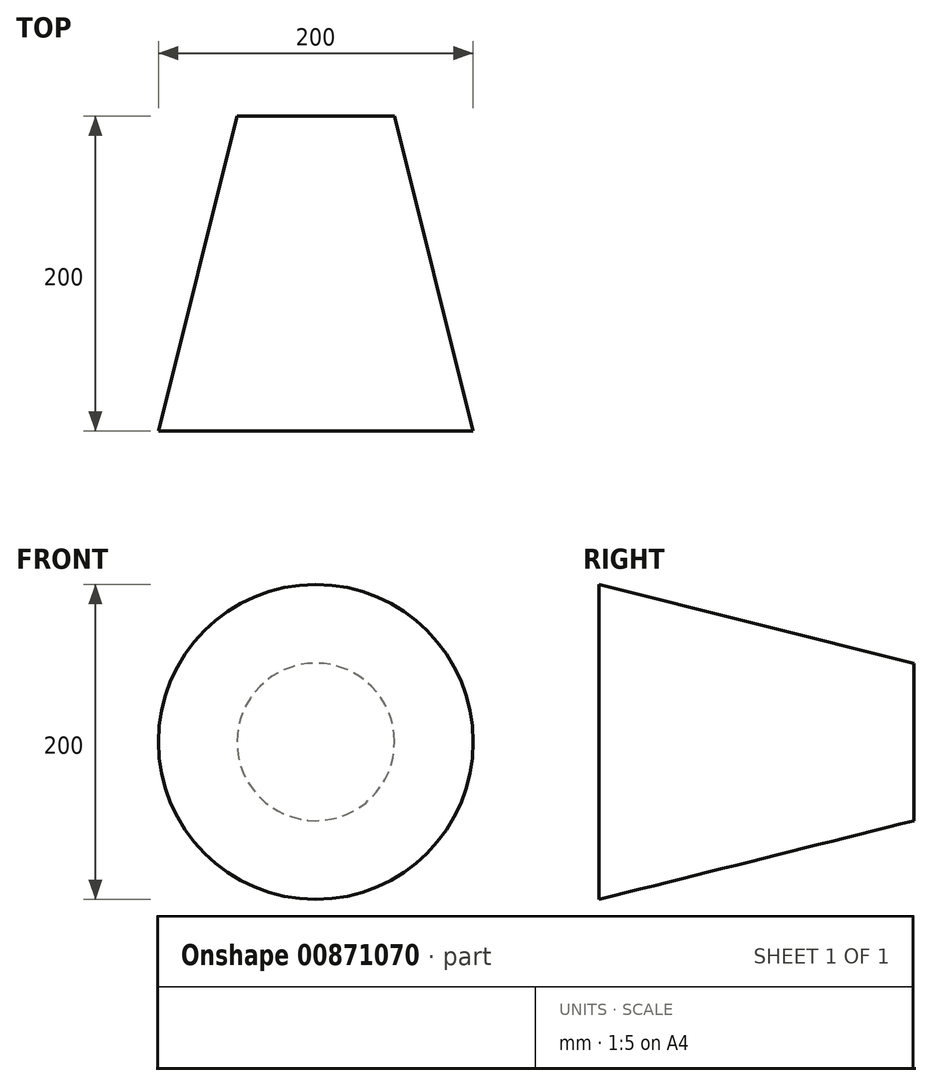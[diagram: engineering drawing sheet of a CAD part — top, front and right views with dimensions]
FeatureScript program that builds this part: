
annotation { "Feature Type Name" : "Feature", "Feature Type Description" : "" }
export const myFeature = defineFeature(function(context is Context, id is Id, definition is map)
    precondition{}
    {
        {
            var Q0;
            Q0=qCreatedBy(makeId("Right.planeOp"),FACE);
            var sketch = newSketch(context, id + "F0", { "sketchPlane" : qUnion([Q0])});
            skLineSegment(sketch, "E0", {"start": v(0, 0) * mm, "end": v(200, 0) * mm});
            skLineSegment(sketch, "E1", {"start": v(200, 0) * mm, "end": v(200, 50) * mm});
            skLineSegment(sketch, "E2", {"start": v(200, 50) * mm, "end": v(0, 100) * mm});
            skLineSegment(sketch, "E3", {"start": v(0, 100) * mm, "end": v(0, 0) * mm});
            skSolve(sketch);
        }
        {
            var Q0;
            Q0 = qSketchRegion(id + "F0", true);
            var Q1;
            Q1=sQuery(id+"F0.wireOp",EDGE,"E0");
            revolve(context, id + "F1", {"surfaceOperationType" : NewSurfaceOperationType.NEW, "entities" : qUnion([Q0]), "axis" : qUnion([Q1]), "revolveType" : RevolveType.FULL});
        }
    });
